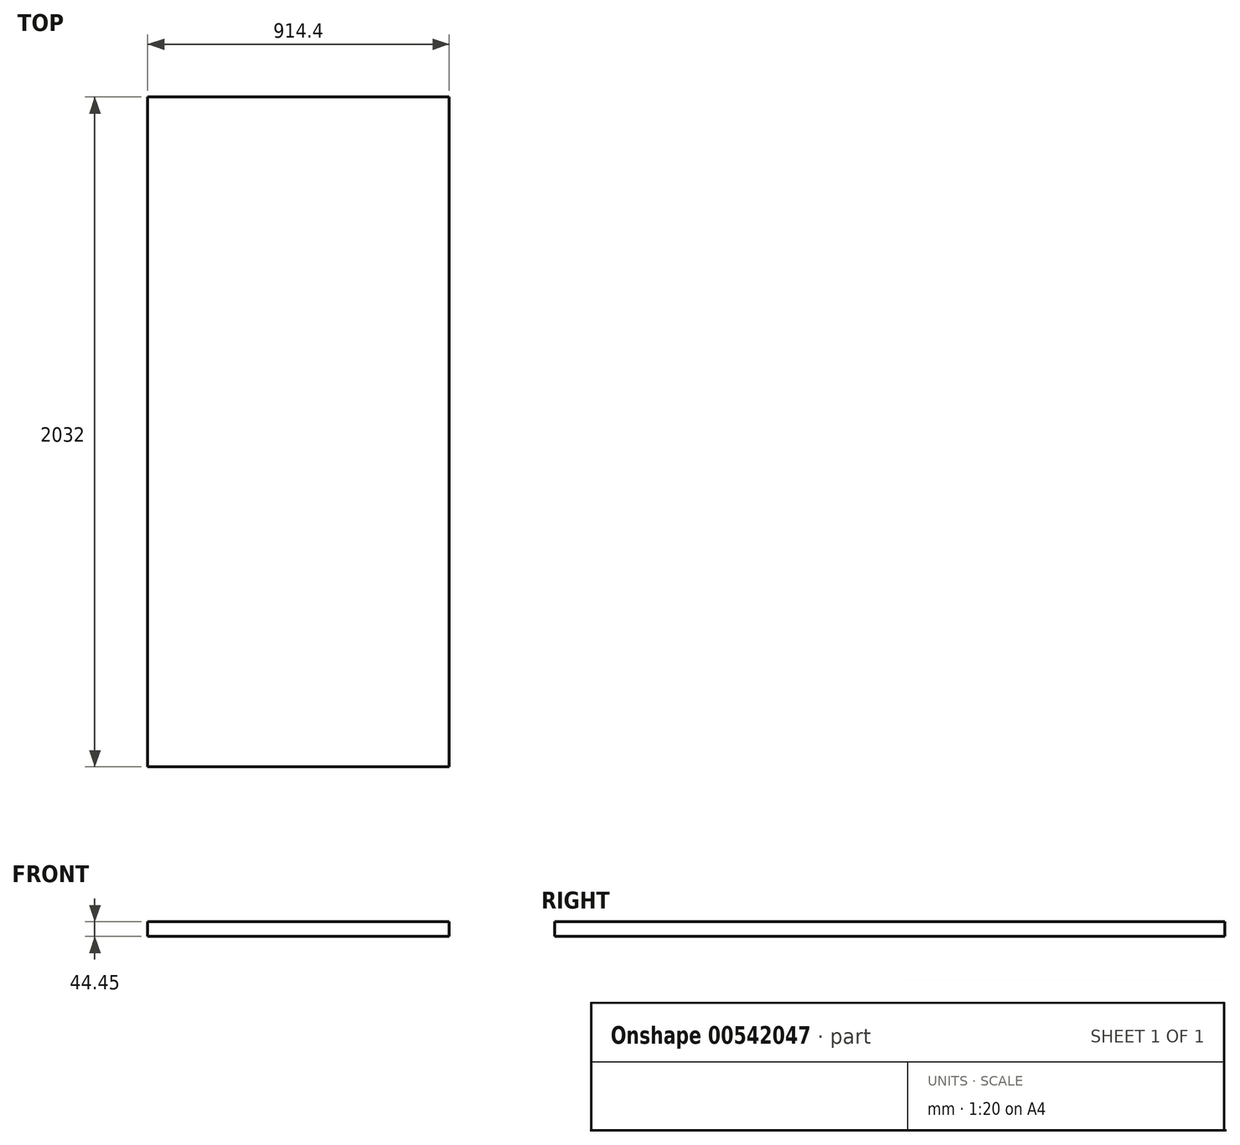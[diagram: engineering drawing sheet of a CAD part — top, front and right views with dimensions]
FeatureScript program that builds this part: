
annotation { "Feature Type Name" : "Feature", "Feature Type Description" : "" }
export const myFeature = defineFeature(function(context is Context, id is Id, definition is map)
    precondition{}
    {
        {
            var Q0;
            Q0=qCreatedBy(makeId("Top.planeOp"),FACE);
            var sketch = newSketch(context, id + "F0", { "sketchPlane" : qUnion([Q0])});
            skLineSegment(sketch, "E0.bottom", {"start": v(-457.2, 1016) * mm, "end": v(457.2, 1016) * mm});
            skLineSegment(sketch, "E0.top", {"start": v(-457.2, -1016) * mm, "end": v(457.2, -1016) * mm});
            skLineSegment(sketch, "E0.left", {"start": v(-457.2, 1016) * mm, "end": v(-457.2, -1016) * mm});
            skLineSegment(sketch, "E0.right", {"start": v(457.2, 1016) * mm, "end": v(457.2, -1016) * mm});
            skPoint(sketch, "E0.middle", {"position": v(0, 0) * mm});
            skSolve(sketch);
        }
        {
            var Q0;
            Q0=makeQuery(id+"F0.imprint","IMPRINT",FACE,{"disambiguationData":[TD([[makeQuery(id+"F0.imprint","IMPRINT",EDGE,{"derivedFrom":sQuery(id+"F0.wireOp",EDGE,"E0.bottom")}),-1.0]])]});
            extrude(context, id + "F1", {"entities" : qUnion([Q0]), "depth" : 44.45 * mm, "offsetDistance" : 25.4 * mm});
        }
    });
